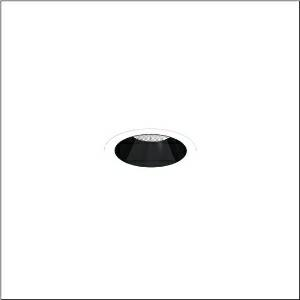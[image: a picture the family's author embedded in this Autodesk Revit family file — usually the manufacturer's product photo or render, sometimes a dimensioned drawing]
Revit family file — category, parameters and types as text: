
# Revit family: lunis_21_m_51db17ec91c
name_source: partatom
category: Lighting Fixtures
units: mm (PartAtom-declared; Revit-internal decimal feet)

## family parameters
Cut with Voids When Loaded = No
Host = Face
Light Source = No
Part Type = Normal
Room Calculation Point = No
Round Connector Dimension = Use Diameter
Shared = No

## types (1)
- --- (1 x LED, 3310 lm, 25.5 W, 6500K)
    Apparent Load = 26 VA
    CIE Flux Codes = 98 100 100 100 100
    Color Rendering = 80
    Color Temperature = 6500K
    Default Elevation = 1800 mm
    Description = Lunis 21,  M, downlight, light control with lens, of PMMA, anti glare with reflector, of PC, light emission: direct distribution, LED rated luminous flux: 1.540lm, light colour: 830/840/865, with terminal, 5-pole, mains connection: 220..240V, AC/DC, 0/50..60Hz, housing, round, of diecast aluminium, traffic white (RAL 9016), diameter: 115mm, clamping range: 1..40mm, protection rating (complete): IP20, protection rating (on room side): IP54, insulation class (complete): insulation class II (safety insulation), certification: CE, impact resistance: IK03, packaging unit: 1 piece
    Height = 0 mm  [stored 0 ft]
    Lamp = 1 x LED
    Lamp Light Flux = 3310 lm
    Lamp Power = 25.5 W
    Lamp count = 1
    Length = 115 mm
    Luminous efficacy = 130 lm/W
    Manufacturer = Siteco
    ModVariant = No
    Model = 51DB17EC91C
    Mounting Place = Ceiling
    Mounting Type = Recessed
    Number of Poles = 1
    OnlyDefault = Yes
    Power Factor = 1
    Product Name = Lunis 21 M
    Product group = downlight
    ProductGroupID = 400
    Protection Class = Protection class II
    Protection Degree = IP 20
    RLX_Detail_Level = 1
    RLX_Emergency_Light_Flux = 0 lm
    RLX_Emergency_Type = 0
    RLX_Emergency_Type_DB = No
    RlxData = <blob elided: 14953 chars, md5=5fcc7db4>
    Socket = socket
    Standby Power = 0 W
    System Light Flux = 3310 lm
    System Power = 26 W
    Type Comments = individual setting: colour temperature 6500K, luminous flux: 100 % | (ON | ON | OFF | OFF) | 700 mA
    Type Image = l_1290854.jpg
    URL = http://relux.com
    VarID = @adj_020054
    Voltage = 0 V
    Weight = 0.00 kg
    Width = 0 mm  [stored 0 ft]

note: [stored X ft] marks values corroborated as IEEE doubles in the binary element streams (Revit-internal decimal feet)

## geometry (parser evidence)
native form markers: Sweep x11
no freeform markers — native parametric forms only
